# Revit family: d4e5b32d_4149_4d59_9c16_d8ee25d3644f
name_source: partatom
category: Lighting Fixtures
revit_build: Autodesk Revit 2015 (Build: 20140903_1530(x64)
units: mm (PartAtom-declared; Revit-internal decimal feet)

## types (1)
- Default
    BIMobject category = Ceiling Mounted
    BIMobject category code = lighting-ceiling-mounted
    BIMobject main category = Lighting
    BIMobject main category code = lighting
    BOSUseNativeGeometries = 1
    Brand url = http://www.kreon.com
    Color Filter = 16777215
    Design country = Belgium
    Dimming Lamp Color Temperature Shift = <None>
    Edition number = 1
    IFC Classification = Lamp
    Light Source Symbol Size = 2' - 0"
    Manufacturer country = Belgium
    Manufacturer name = Kreon
    Material main = Aluminium
    Material secondary = Glass
    NBS Reference Code = 70-80
    NBS Reference Description = Lighting Systems
    OmniClass Code = 23-35 47 11 21 15
    OmniClass Description = Lighting Posts
    Product Guid = 8ac85c2a-4722-481f-850b-c5f6d683bf5d
    Product SKU = kr_down_inline_165
    Product data url = https://bimobject.com
    Product family = Lighting
    Product group = recessed downlight luminaires
    Product name = down in-line 165
    Product url = https://www.kreon.com
    QR code = http://bimobject.com
    Technical description = https://www.kreon.com
    Uniclass 1.4 Code = L7474
    Uniclass 1.4 Description = Lamps
    Uniclass 2.0 Code = SS-70-80
    Uniclass 2.0 Description = Lighting Systems
    Uniclass 2015 Code = Ss_70_80
    Uniclass 2015 Name = Lighting systems

## geometry (parser evidence)
native form markers: Sweep x2
no freeform markers — native parametric forms only
